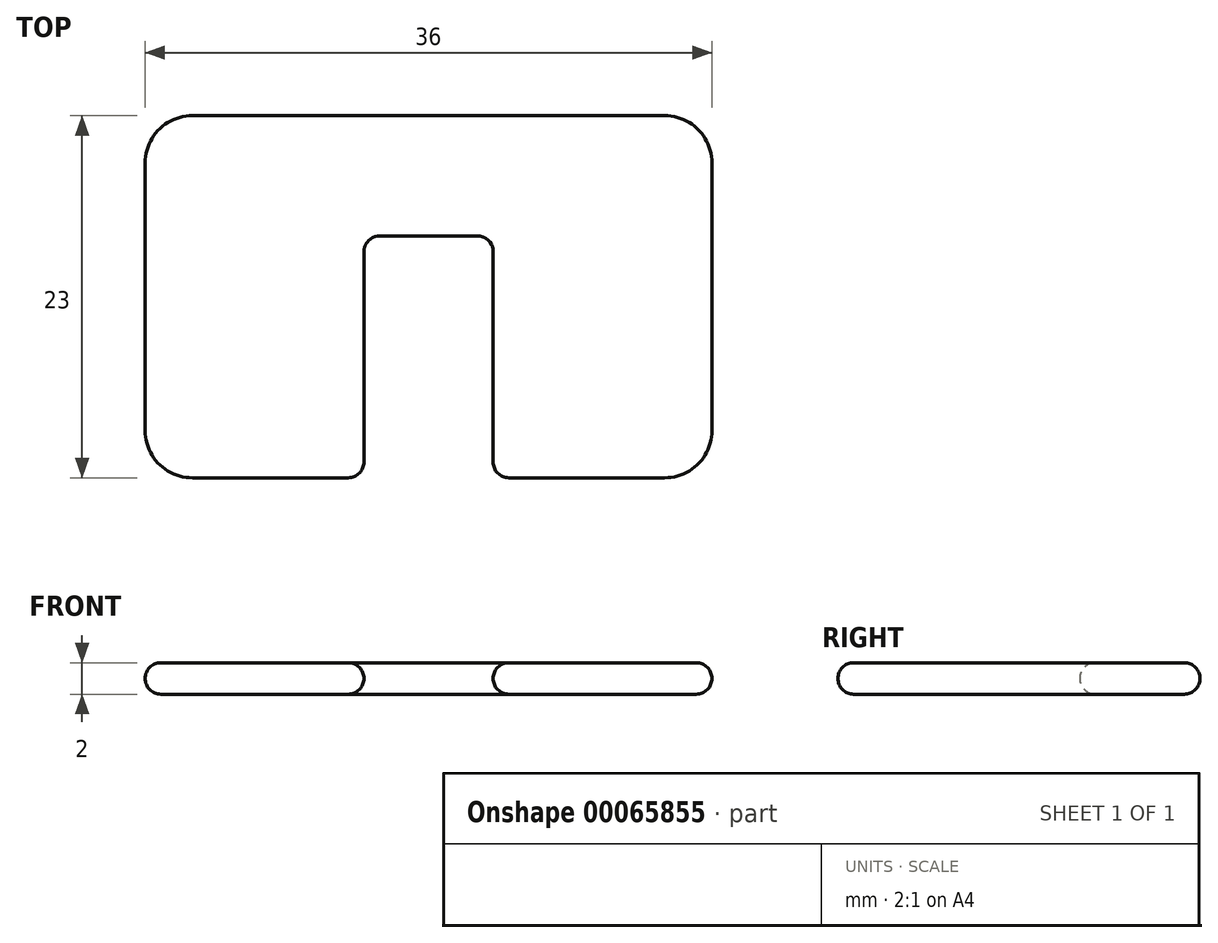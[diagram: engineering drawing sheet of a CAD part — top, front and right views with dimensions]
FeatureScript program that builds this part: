
annotation { "Feature Type Name" : "Feature", "Feature Type Description" : "" }
export const myFeature = defineFeature(function(context is Context, id is Id, definition is map)
    precondition{}
    {
        {
            var Q0;
            Q0=qCreatedBy(makeId("Top.planeOp"),FACE);
            var sketch = newSketch(context, id + "F0", { "sketchPlane" : qUnion([Q0])});
            skLineSegment(sketch, "E0.bottom", {"start": v(4.1, -15) * mm, "end": v(-4.1, -15) * mm});
            skLineSegment(sketch, "E0.top", {"start": v(15, 15) * mm, "end": v(-15, 15) * mm});
            skLineSegment(sketch, "E0.left", {"start": v(18, -5) * mm, "end": v(18, 12) * mm});
            skLineSegment(sketch, "E0.right", {"start": v(-18, -5) * mm, "end": v(-18, 12) * mm});
            skPoint(sketch, "E0.middle", {"position": v(0, 0) * mm});
            skLineSegment(sketch, "E1.bottom", {"start": v(-4.1, -15) * mm, "end": v(4.1, -15) * mm});
            skLineSegment(sketch, "E1.top", {"start": v(-4.1, 7.36) * mm, "end": v(4.1, 7.36) * mm});
            skLineSegment(sketch, "E1.left", {"start": v(-4.1, -8) * mm, "end": v(-4.1, 7.36) * mm});
            skLineSegment(sketch, "E1.right", {"start": v(4.1, -8) * mm, "end": v(4.1, 7.36) * mm});
            skLineSegment(sketch, "E2", {"start": v(-15, -8) * mm, "end": v(15, -8) * mm});
            skPoint(sketch, "E3.orphan", {"position": v(-18, -15) * mm});
            skPoint(sketch, "E4.orphan", {"position": v(18, -15) * mm});
            skPoint(sketch, "E5.visualSharp", {"position": v(-18, 15) * mm});
            skArc(sketch, "E5.filletArc", {"start": v(-15, 15) * mm, "mid": v(-17.12, 14.12) * mm, "end": v(-18, 12) * mm});
            skPoint(sketch, "E6.visualSharp", {"position": v(-18, -8) * mm});
            skArc(sketch, "E6.filletArc", {"start": v(-18, -5) * mm, "mid": v(-17.12, -7.12) * mm, "end": v(-15, -8) * mm});
            skPoint(sketch, "E7.visualSharp", {"position": v(18, 15) * mm});
            skArc(sketch, "E7.filletArc", {"start": v(18, 12) * mm, "mid": v(17.12, 14.12) * mm, "end": v(15, 15) * mm});
            skPoint(sketch, "E8.visualSharp", {"position": v(18, -8) * mm});
            skArc(sketch, "E8.filletArc", {"start": v(15, -8) * mm, "mid": v(17.12, -7.12) * mm, "end": v(18, -5) * mm});
            skSolve(sketch);
        }
        {
            var Q0;
            Q0=makeQuery(id+"F0.imprint","IMPRINT",FACE,{"disambiguationData":[TD([[makeQuery(id+"F0.imprint","IMPRINT",EDGE,{"derivedFrom":sQuery(id+"F0.wireOp",EDGE,"E0.top")}),1.0]])]});
            extrude(context, id + "F1", {"entities" : qUnion([Q0]), "depth" : 2 * mm});
        }
        {
            var Q0;
            Q0=makeQuery(id+"F1.opExtrude","SWEPT_EDGE",EDGE,{"disambiguationData":[OSD([sQuery(id+"F0.wireOp",EDGE,"E0.bottom"),sQuery(id+"F0.wireOp",EDGE,"E0.right")])]});
            var Q1;
            Q1=makeQuery(id+"F1.opExtrude","CAP_FACE",FACE,{"disambiguationData":[OSD([sQuery(id+"F0.wireOp",EDGE,"E0.bottom"),sQuery(id+"F0.wireOp",EDGE,"E0.top"),sQuery(id+"F0.wireOp",EDGE,"E0.left"),sQuery(id+"F0.wireOp",EDGE,"E0.right"),sQuery(id+"F0.wireOp",EDGE,"E1.top"),sQuery(id+"F0.wireOp",EDGE,"E1.left"),sQuery(id+"F0.wireOp",EDGE,"E1.right")])],"isStart":true});
            var Q2;
            Q2=makeQuery(id+"F1.opExtrude","CAP_FACE",FACE,{"disambiguationData":[OSD([sQuery(id+"F0.wireOp",EDGE,"E0.bottom"),sQuery(id+"F0.wireOp",EDGE,"E0.top"),sQuery(id+"F0.wireOp",EDGE,"E0.left"),sQuery(id+"F0.wireOp",EDGE,"E0.right"),sQuery(id+"F0.wireOp",EDGE,"E1.top"),sQuery(id+"F0.wireOp",EDGE,"E1.left"),sQuery(id+"F0.wireOp",EDGE,"E1.right")])],"isStart":false});
            var Q3;
            Q3=makeQuery(id+"F1.opExtrude","SWEPT_EDGE",EDGE,{"disambiguationData":[OSD([sQuery(id+"F0.wireOp",EDGE,"E0.top"),sQuery(id+"F0.wireOp",EDGE,"E0.right")])]});
            var Q4;
            {var subQ0=sQuery(id+"F0.wireOp",EDGE,"E0.bottom");Q4=makeQuery(id+"F1.opExtrude","SWEPT_FACE",FACE,{"disambiguationData":[OSD([subQ0]),TDD([makeQuery(id+"F0.imprint","IMPRINT",EDGE,{"disambiguationData":[TD([[makeQuery(id+"F0.imprint","INTERSECT",VERTEX,{"derivedFrom":[subQ0,sQuery(id+"F0.wireOp",EDGE,"E0.right")]}),1.0]])],"derivedFrom":subQ0})])]});}
            var Q5;
            Q5=makeQuery(id+"F1.opExtrude","SWEPT_EDGE",EDGE,{"disambiguationData":[OSD([sQuery(id+"F0.wireOp",EDGE,"E0.bottom"),sQuery(id+"F0.wireOp",EDGE,"E1.bottom"),sQuery(id+"F0.wireOp",EDGE,"E1.left")])]});
            var Q6;
            Q6=makeQuery(id+"F1.opExtrude","SWEPT_FACE",FACE,{"disambiguationData":[OSD([sQuery(id+"F0.wireOp",EDGE,"E0.top")])]});
            var Q7;
            {var subQ0=sQuery(id+"F0.wireOp",EDGE,"E0.bottom");Q7=makeQuery(id+"F1.opExtrude","SWEPT_FACE",FACE,{"disambiguationData":[OSD([subQ0]),TDD([makeQuery(id+"F0.imprint","IMPRINT",EDGE,{"disambiguationData":[TD([[makeQuery(id+"F0.imprint","INTERSECT",VERTEX,{"derivedFrom":[subQ0,sQuery(id+"F0.wireOp",EDGE,"E0.left")]}),-1.0]])],"derivedFrom":subQ0})])]});}
            var Q8;
            Q8=makeQuery(id+"F1.opExtrude","SWEPT_EDGE",EDGE,{"disambiguationData":[OSD([sQuery(id+"F0.wireOp",EDGE,"E0.bottom"),sQuery(id+"F0.wireOp",EDGE,"E0.left")])]});
            var Q9;
            Q9=makeQuery(id+"F1.opExtrude","CAP_EDGE",EDGE,{"disambiguationData":[OSD([sQuery(id+"F0.wireOp",EDGE,"E0.left")])],"isStart":false});
            var Q10;
            Q10=makeQuery(id+"F1.opExtrude","CAP_EDGE",EDGE,{"disambiguationData":[OSD([sQuery(id+"F0.wireOp",EDGE,"E0.left")])],"isStart":true});
            var Q11;
            Q11=makeQuery(id+"F1.opExtrude","CAP_EDGE",EDGE,{"disambiguationData":[OSD([sQuery(id+"F0.wireOp",EDGE,"E0.top")])],"isStart":false});
            var Q12;
            Q12=makeQuery(id+"F1.opExtrude","SWEPT_FACE",FACE,{"disambiguationData":[OSD([sQuery(id+"F0.wireOp",EDGE,"E0.left")])]});
            var Q13;
            Q13=makeQuery(id+"F1.opExtrude","SWEPT_EDGE",EDGE,{"disambiguationData":[OSD([sQuery(id+"F0.wireOp",EDGE,"E0.bottom"),sQuery(id+"F0.wireOp",EDGE,"E1.bottom"),sQuery(id+"F0.wireOp",EDGE,"E1.right")])]});
            var Q14;
            Q14=makeQuery(id+"F1.opExtrude","SWEPT_FACE",FACE,{"disambiguationData":[OSD([sQuery(id+"F0.wireOp",EDGE,"E0.right")])]});
            var Q15;
            Q15=makeQuery(id+"F1.opExtrude","SWEPT_EDGE",EDGE,{"disambiguationData":[OSD([sQuery(id+"F0.wireOp",EDGE,"E1.top"),sQuery(id+"F0.wireOp",EDGE,"E1.right")])]});
            var Q16;
            Q16=makeQuery(id+"F1.opExtrude","SWEPT_FACE",FACE,{"disambiguationData":[OSD([sQuery(id+"F0.wireOp",EDGE,"E1.top")])]});
            var Q17;
            Q17=makeQuery(id+"F1.opExtrude","SWEPT_FACE",FACE,{"disambiguationData":[OSD([sQuery(id+"F0.wireOp",EDGE,"E1.left")])]});
            var Q18;
            Q18=makeQuery(id+"F1.opExtrude","SWEPT_FACE",FACE,{"disambiguationData":[OSD([sQuery(id+"F0.wireOp",EDGE,"E1.right")])]});
            var Q19;
            Q19=makeQuery(id+"F1.opExtrude","CAP_EDGE",EDGE,{"disambiguationData":[OSD([sQuery(id+"F0.wireOp",EDGE,"E0.right")])],"isStart":true});
            var Q20;
            Q20=makeQuery(id+"F1.opExtrude","CAP_EDGE",EDGE,{"disambiguationData":[OSD([sQuery(id+"F0.wireOp",EDGE,"E1.left")])],"isStart":false});
            var Q21;
            Q21=makeQuery(id+"F1.opExtrude","SWEPT_EDGE",EDGE,{"disambiguationData":[OSD([sQuery(id+"F0.wireOp",EDGE,"E1.top"),sQuery(id+"F0.wireOp",EDGE,"E1.left")])]});
            var Q22;
            Q22=makeQuery(id+"F1.opExtrude","SWEPT_EDGE",EDGE,{"disambiguationData":[OSD([sQuery(id+"F0.wireOp",EDGE,"E0.top"),sQuery(id+"F0.wireOp",EDGE,"E0.left")])]});
            var Q23;
            {var subQ0=sQuery(id+"F0.wireOp",EDGE,"E0.bottom");Q23=makeQuery(id+"F1.opExtrude","CAP_EDGE",EDGE,{"disambiguationData":[OSD([subQ0]),TDD([makeQuery(id+"F0.imprint","IMPRINT",EDGE,{"disambiguationData":[TD([[makeQuery(id+"F0.imprint","INTERSECT",VERTEX,{"derivedFrom":[subQ0,sQuery(id+"F0.wireOp",EDGE,"E0.left")]}),-1.0]])],"derivedFrom":subQ0})])],"isStart":true});}
            var Q24;
            {var subQ0=sQuery(id+"F0.wireOp",EDGE,"E0.bottom");Q24=makeQuery(id+"F1.opExtrude","CAP_EDGE",EDGE,{"disambiguationData":[OSD([subQ0]),TDD([makeQuery(id+"F0.imprint","IMPRINT",EDGE,{"disambiguationData":[TD([[makeQuery(id+"F0.imprint","INTERSECT",VERTEX,{"derivedFrom":[subQ0,sQuery(id+"F0.wireOp",EDGE,"E0.left")]}),-1.0]])],"derivedFrom":subQ0})])],"isStart":false});}
            var Q25;
            {var subQ0=sQuery(id+"F0.wireOp",EDGE,"E0.bottom");Q25=makeQuery(id+"F1.opExtrude","CAP_EDGE",EDGE,{"disambiguationData":[OSD([subQ0]),TDD([makeQuery(id+"F0.imprint","IMPRINT",EDGE,{"disambiguationData":[TD([[makeQuery(id+"F0.imprint","INTERSECT",VERTEX,{"derivedFrom":[subQ0,sQuery(id+"F0.wireOp",EDGE,"E0.right")]}),1.0]])],"derivedFrom":subQ0})])],"isStart":true});}
            var Q26;
            {var subQ0=sQuery(id+"F0.wireOp",EDGE,"E0.bottom");Q26=makeQuery(id+"F1.opExtrude","CAP_EDGE",EDGE,{"disambiguationData":[OSD([subQ0]),TDD([makeQuery(id+"F0.imprint","IMPRINT",EDGE,{"disambiguationData":[TD([[makeQuery(id+"F0.imprint","INTERSECT",VERTEX,{"derivedFrom":[subQ0,sQuery(id+"F0.wireOp",EDGE,"E0.right")]}),1.0]])],"derivedFrom":subQ0})])],"isStart":false});}
            var Q27;
            Q27=makeQuery(id+"F1.opExtrude","CAP_EDGE",EDGE,{"disambiguationData":[OSD([sQuery(id+"F0.wireOp",EDGE,"E0.top")])],"isStart":true});
            var Q28;
            Q28=makeQuery(id+"F1.opExtrude","CAP_EDGE",EDGE,{"disambiguationData":[OSD([sQuery(id+"F0.wireOp",EDGE,"E0.right")])],"isStart":false});
            var Q29;
            Q29=makeQuery(id+"F1.opExtrude","CAP_EDGE",EDGE,{"disambiguationData":[OSD([sQuery(id+"F0.wireOp",EDGE,"E1.top")])],"isStart":true});
            var Q30;
            Q30=makeQuery(id+"F1.opExtrude","CAP_EDGE",EDGE,{"disambiguationData":[OSD([sQuery(id+"F0.wireOp",EDGE,"E1.top")])],"isStart":false});
            var Q31;
            Q31=makeQuery(id+"F1.opExtrude","CAP_EDGE",EDGE,{"disambiguationData":[OSD([sQuery(id+"F0.wireOp",EDGE,"E1.left")])],"isStart":true});
            var Q32;
            Q32=makeQuery(id+"F1.opExtrude","CAP_EDGE",EDGE,{"disambiguationData":[OSD([sQuery(id+"F0.wireOp",EDGE,"E1.right")])],"isStart":true});
            var Q33;
            Q33=makeQuery(id+"F1.opExtrude","CAP_EDGE",EDGE,{"disambiguationData":[OSD([sQuery(id+"F0.wireOp",EDGE,"E1.right")])],"isStart":false});
            fillet(context, id + "F2", {"entities" : qUnion([Q0, Q1, Q2, Q3, Q4, Q5, Q6, Q7, Q8, Q9, Q10, Q11, Q12, Q13, Q14, Q15, Q16, Q17, Q18, Q19, Q20, Q21, Q22, Q23, Q24, Q25, Q26, Q27, Q28, Q29, Q30, Q31, Q32, Q33]), "radius" : 1 * mm, "tangentPropagation" : true, "allowEdgeOverflow" : false});
        }
    });
